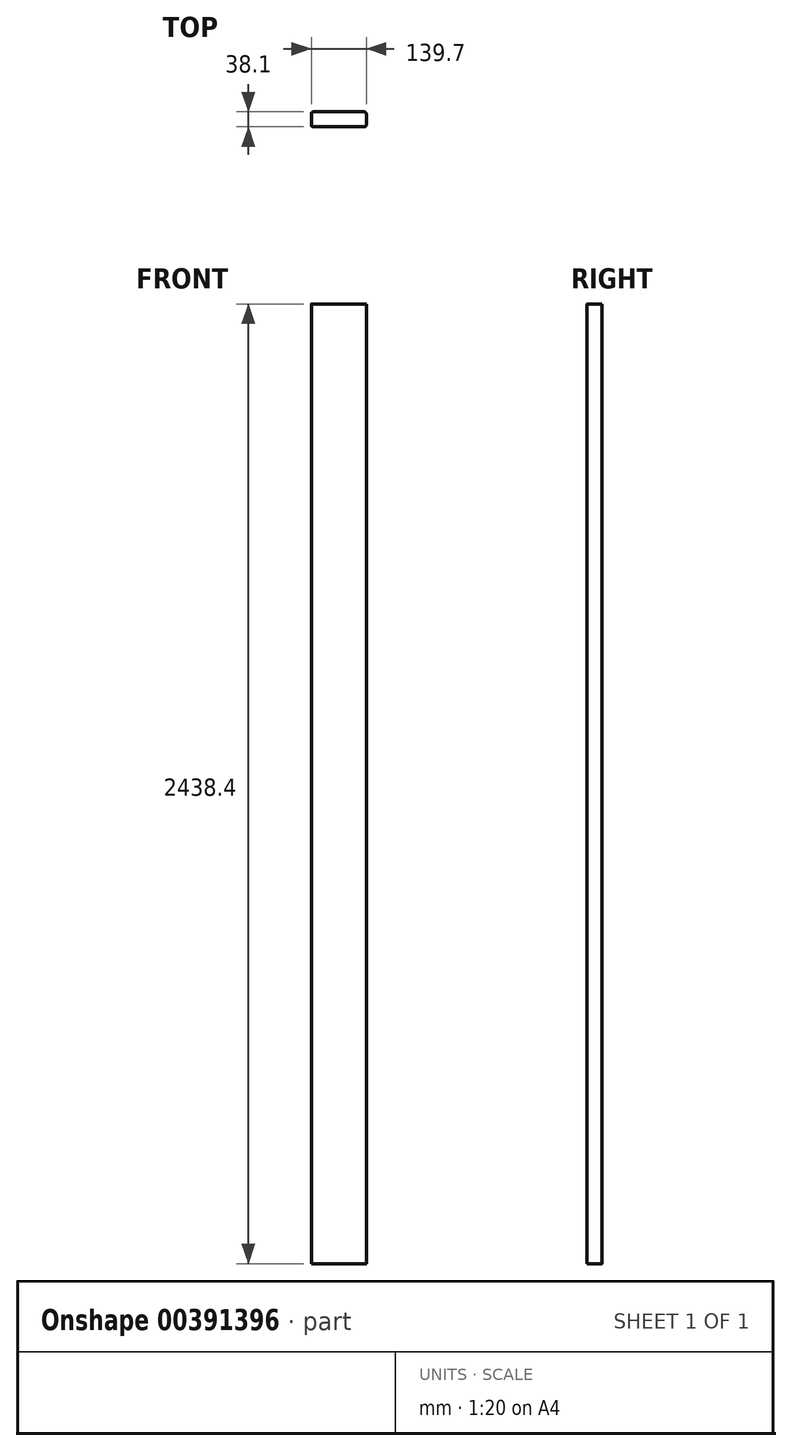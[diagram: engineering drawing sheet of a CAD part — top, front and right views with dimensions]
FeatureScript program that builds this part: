
annotation { "Feature Type Name" : "Feature", "Feature Type Description" : "" }
export const myFeature = defineFeature(function(context is Context, id is Id, definition is map)
    precondition{}
    {
        {
            var Q0;
            Q0=qCreatedBy(makeId("Top.planeOp"),FACE);
            var sketch = newSketch(context, id + "F0", { "sketchPlane" : qUnion([Q0])});
            skLineSegment(sketch, "E0.bottom", {"start": v(5.08, 0.27) * mm, "end": v(134.62, 0.27) * mm});
            skLineSegment(sketch, "E0.top", {"start": v(5.08, 38.37) * mm, "end": v(134.62, 38.37) * mm});
            skLineSegment(sketch, "E0.left", {"start": v(0, 5.35) * mm, "end": v(0, 33.29) * mm});
            skLineSegment(sketch, "E0.right", {"start": v(139.7, 5.35) * mm, "end": v(139.7, 33.29) * mm});
            skPoint(sketch, "E1.visualSharp", {"position": v(0, 38.37) * mm});
            skArc(sketch, "E1.filletArc", {"start": v(5.08, 38.37) * mm, "mid": v(1.49, 36.88) * mm, "end": v(0, 33.29) * mm});
            skPoint(sketch, "E2.visualSharp", {"position": v(0, 0.27) * mm});
            skArc(sketch, "E2.filletArc", {"start": v(0, 5.35) * mm, "mid": v(1.49, 1.76) * mm, "end": v(5.08, 0.27) * mm});
            skPoint(sketch, "E3.visualSharp", {"position": v(139.7, 0.27) * mm});
            skArc(sketch, "E3.filletArc", {"start": v(134.62, 0.27) * mm, "mid": v(138.21, 1.76) * mm, "end": v(139.7, 5.35) * mm});
            skPoint(sketch, "E4.visualSharp", {"position": v(139.7, 38.37) * mm});
            skArc(sketch, "E4.filletArc", {"start": v(139.7, 33.29) * mm, "mid": v(138.21, 36.88) * mm, "end": v(134.62, 38.37) * mm});
            skSolve(sketch);
        }
        {
            var Q0;
            Q0 = qSketchRegion(id + "F0", true);
            extrude(context, id + "F1", {"entities" : qUnion([Q0]), "depth" : 2438.4 * mm});
        }
    });
